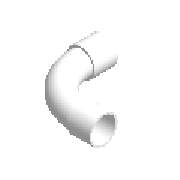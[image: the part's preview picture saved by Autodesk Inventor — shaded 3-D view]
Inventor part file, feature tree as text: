
AUTODESK INVENTOR PART (.ipt)
format: ipt  version: 2023 (Build 270158000, 158)  size: 223,232 bytes
history: native  units: mm (DEFAULTED — no unit token found)
features: other x6, sketch x2, revolve x2, sweep x1
ambient origin geometry x8: Origin, YZ Plane, XZ Plane, XY Plane, X Axis, Y Axis, Z Axis, Center Point
bodies: Solid1 (feature_tree)
feature tree (11):
  sketch  "Sketch1"  dims[d3=90.0deg d0=160.0mm]
  revolve  "Revolution1"  [1 undecoded]
  sweep  "Sweep1"
  revolve  "Revolution2"  [1 undecoded]
  other  "Work Point18"
  other  "Work Point19"
  other  "Work Axis30"
  other  "Work Point20"
  other  "Work Axis31"
  other  "Work Point21"
  sketch  "Sketch2"  dims[d1=11.9mm d2=86.0mm d4=136.2mm d5=0.0mm d6=160.0mm d7=136.2mm d8=308.1mm d9=308.1mm d160=90.0deg d10=11.9mm d11=11.9mm d12=86.0mm d13=160.0mm d14=320.0mm d15=320.0mm d16=11.9mm d192=0.0mm]
note: 2 required parameter values undecoded (feature->parameter linkage not recoverable at this tier; creation-order binding heuristic only, values carry confidence <= 0.55)
